# Revit family: IS_ConnectSpace_E1190_BIM_DE
name_source: partatom
category: Plumbing Fixtures
revit_build: Autodesk Revit MEP 2016 (Build: 20161004_0715(x64)
units: mm (PartAtom-declared; Revit-internal decimal feet)

## family parameters
Always vertical = No
Cut with Voids When Loaded = No
OmniClass Number = 23.45.05.14.27
OmniClass Title = Bidets
Part Type = Normal
Room Calculation Point = No
Round Connector Dimension = Use Diameter
Shared = No
Work Plane-Based = No

## types (2) — shared parameters
Accessories = www.idealstandard.de\ersatzteile
AreaUnits = millimeters
AssetType = Fixed
BIMobject category = Bidets
BOSUseNativeGeometries = 1
Brand = Ideal Standard
Brand url = http://www.idealstandard.co.uk
CodePerformance = DIN EN 14528 CL 15, DIN EN 35
ConnectionType = Plumbing
CurrencyUnit = €
CurrentRevision = 1
Date of publishing = 2017_11_20
DurationUnit = year
Edition number = 1
ExpectedLife = 25
Features = CONNECT SPACE compact wall mounted bidet 360x480mm, 1 taphole
IFC Classification = Sanitary Terminal
IfcExportAs = IfcSanitaryTerminalType
IfcExportType = BIDETS
Installation instructions = http://www.idealstandard.de
InstallationInstructions = www.idealstandard.de\produkte
LinearUnits = millimeters
Manufacturer name = Ideal Standard
ManufacturerURL = www.idealstandard.com
Material = Vitreous china
Material main = Ceramics
NBS Reference Code = 35-06-11
NBS Reference Description = Bidets
Nominal height = 305
Nominal width = 360
NominalDepth = 481 mm  [stored 1.57808 ft]
NominalHeight = 340 mm
NominalLength = 481 mm  [stored 1.57808 ft]
NominalWidth = 364 mm
OmniClass Code = 23-31 23 00
OmniClass Description = Bidets
Product Guid = 97394f6d-1a13-44a5-9dc6-6614d27896ca
Product SKU = E1190
Product certification = DIN EN 14528 CL 15, DIN EN 35
Product data url = https://bimobject.com
Product family = CONNECT SPACE
Product group = Bidet
Product name = CONNECT SPACE compact wall mounted bidet 360x480mm, 1 taphole
Product url = http://www.idealstandard.de
ProductInformation = www.idealstandard.de/produkte
QR code = http://bimobject.com
Shape = Sculptured
Size = 364x481x340 mm
Space = Internal
SpareParts = www.idealstandard.de/ersatzteile
Technical description = http://www.idealstandard.de
URL = http://www.idealstandard.de
Uniclass 2.0 Code = PR-35-06-11
Uniclass 2.0 Description = Bidets
Uniclass 2015 Code = Pr_40_20_06_11
Uniclass 2015 Name = Bidets
Uniclass2015Code = Pr_40_20_06_11
Uniclass2015Title = Bidets
Uniclass2015Version = Products v1.1
Version = 1
VolumeUnits = Litres
Weight Net (Kg) = 17.5
zero-valued in all types: Cost, DrainSize

## per-type parameters (varying)
| type | BIMObjectName | BarCode | Color | EAN code | Finish | MainColor | Model | ModelNumber | Name | NettWeight |
| E119001 CONNECT SPACE compact wall mounted bidet 360x480mm, 1 taphole | ISI_IdealStandard_Bidets_ConnectSpace_E119001 | 5017830447979 | White | 5017830447979 | White | White | E119001 | E119001 | Bidets_ConnectSpace_E119001_IdealStandard | 17,5 kg |
| E1190MA CONNECT SPACE compact wall mounted bidet 360x480mm, 1 taphole | ISI_IdealStandard_Bidets_ConnectSpace_E1190MA | 5017830451228 | WHITE IP | 5017830451228 | WHITE IP | WHITE IP | E1190MA | E1190MA | Bidets_ConnectSpace_E1190MA_IdealStandard | 18 kg |

note: column(s) folded — value = type name in every type: Description, ModelReference

note: [stored X ft] marks values corroborated as IEEE doubles in the binary element streams (Revit-internal decimal feet)

## geometry (parser evidence)
native form markers: Blend x4, Sweep x1
no freeform markers — native parametric forms only
